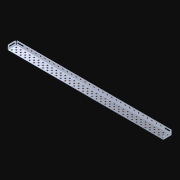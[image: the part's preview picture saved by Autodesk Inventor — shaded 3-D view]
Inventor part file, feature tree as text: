
AUTODESK INVENTOR PART (.ipt)
format: ipt  version: 2021 (Build 250183000, 183)  size: 2,035,200 bytes
history: native  units: in
note: dims shown in document units (in); Inventor stores cm internally (conversion verified against a paired STEP export)
features: other x136, extrude x135, pattern_linear x3, imported_body x1
ambient origin geometry x8: Origin, YZ Plane, XZ Plane, XY Plane, X Axis, Y Axis, Z Axis, Center Point
bodies: Body1 (feature_tree), Body2 (feature_tree), Body3 (feature_tree), Body4 (feature_tree), Body5 (feature_tree), Body6 (feature_tree), Body7 (feature_tree), Body8 (feature_tree), Body9 (feature_tree), Body10 (feature_tree), Body11 (feature_tree), Body12 (feature_tree), Body13 (feature_tree), Body14 (feature_tree), Body15 (feature_tree), Body16 (feature_tree), Body17 (feature_tree), Body18 (feature_tree), Body19 (feature_tree), Body20 (feature_tree), Body21 (feature_tree), Body22 (feature_tree), Body23 (feature_tree), Body24 (feature_tree), Body25 (feature_tree), Body26 (feature_tree), Body27 (feature_tree), Body28 (feature_tree), Body29 (feature_tree), Body30 (feature_tree), Body31 (feature_tree), Body32 (feature_tree), Body33 (feature_tree), Body34 (feature_tree), Body35 (feature_tree), Body36 (feature_tree), Body37 (feature_tree), Body38 (feature_tree), Body39 (feature_tree), Body40 (feature_tree), Body41 (feature_tree), Body42 (feature_tree), Body43 (feature_tree), Body44 (feature_tree), Body45 (feature_tree), Body46 (feature_tree), Body47 (feature_tree), Body48 (feature_tree), Body49 (feature_tree), Body50 (feature_tree), Body51 (feature_tree), Body52 (feature_tree), Body53 (feature_tree), Body54 (feature_tree), Body55 (feature_tree), Body56 (feature_tree), Body57 (feature_tree), Body58 (feature_tree), Body59 (feature_tree), Body60 (feature_tree), Body61 (feature_tree), Body62 (feature_tree), Body63 (feature_tree), Body64 (feature_tree), Body65 (feature_tree), Body66 (feature_tree), Body67 (feature_tree), Body68 (feature_tree), Body69 (feature_tree), Body70 (feature_tree), Body71 (feature_tree), Body72 (feature_tree), Body73 (feature_tree), Body74 (feature_tree), Body75 (feature_tree), Body76 (feature_tree), Body77 (feature_tree), Body78 (feature_tree), Body79 (feature_tree), Body80 (feature_tree), Body81 (feature_tree), Body82 (feature_tree), Body83 (feature_tree), Body84 (feature_tree), Body85 (feature_tree), Body86 (feature_tree), Body87 (feature_tree), Body88 (feature_tree), Body89 (feature_tree), Body90 (feature_tree), Body91 (feature_tree), Body92 (feature_tree), Body93 (feature_tree), Body94 (feature_tree), Body95 (feature_tree), Body96 (feature_tree), Body97 (feature_tree), Body98 (feature_tree), Body99 (feature_tree), Body100 (feature_tree), Body101 (feature_tree), Body102 (feature_tree), Body103 (feature_tree), Body104 (feature_tree), Body105 (feature_tree), Body106 (feature_tree), Body107 (feature_tree), Body108 (feature_tree), Body109 (feature_tree), Body110 (feature_tree), Body111 (feature_tree), Body112 (feature_tree), Body113 (feature_tree), Body114 (feature_tree), Body115 (feature_tree), Body116 (feature_tree), Body117 (feature_tree), Body118 (feature_tree), Body119 (feature_tree), Body120 (feature_tree), Body121 (feature_tree), Body122 (feature_tree), Body123 (feature_tree), Body124 (feature_tree), Body125 (feature_tree), Body126 (feature_tree), Body127 (feature_tree), Body128 (feature_tree), Body129 (feature_tree), Body130 (feature_tree), Body131 (feature_tree), Body132 (feature_tree), Body133 (feature_tree), Body134 (feature_tree), Body135 (feature_tree), Body136 (feature_tree)
feature tree (275):
  parser-record x1  (decoder bookkeeping rows leaked as tree rows — omitted from the tree; the rows remain in map.json)
  imported_body  "Base1"
  pattern_linear  "Rectangular Pattern1"  Spacing1=0.046in  [1 undecoded]
  pattern_linear  "Rectangular Pattern2"  Count1=35 Spacing1=0.5in
  pattern_linear  "Rectangular Pattern3"  Count1=2 Spacing1=0.5in
  other  "Srf1"
  other  "Srf2"
  other  "Srf3"
  other  "Srf4"
  other  "Srf5"
  other  "Srf6"
  other  "Srf7"
  other  "Srf8"
  other  "Srf9"
  other  "Srf10"
  other  "Srf11"
  other  "Srf12"
  other  "Srf13"
  other  "Srf14"
  other  "Srf15"
  other  "Srf16"
  other  "Srf17"
  other  "Srf18"
  other  "Srf19"
  other  "Srf20"
  other  "Srf21"
  other  "Srf22"
  other  "Srf23"
  other  "Srf24"
  other  "Srf25"
  other  "Srf26"
  other  "Srf27"
  other  "Srf28"
  other  "Srf29"
  other  "Srf30"
  other  "Srf31"
  other  "Srf32"
  other  "Srf33"
  other  "Srf34"
  other  "Srf35"
  other  "Srf36"
  other  "Srf37"
  other  "Srf38"
  other  "Srf39"
  other  "Srf40"
  other  "Srf41"
  other  "Srf42"
  other  "Srf43"
  other  "Srf44"
  other  "Srf45"
  other  "Srf46"
  other  "Srf47"
  other  "Srf48"
  other  "Srf49"
  other  "Srf50"
  other  "Srf51"
  other  "Srf52"
  other  "Srf53"
  other  "Srf54"
  other  "Srf55"
  other  "Srf56"
  other  "Srf57"
  other  "Srf58"
  other  "Srf59"
  other  "Srf60"
  other  "Srf61"
  other  "Srf62"
  other  "Srf63"
  other  "Srf64"
  other  "Srf65"
  other  "Srf66"
  other  "Srf67"
  other  "Srf68"
  other  "Srf69"
  other  "Srf70"
  other  "Srf71"
  other  "Srf72"
  other  "Srf73"
  other  "Srf74"
  other  "Srf75"
  other  "Srf76"
  other  "Srf77"
  other  "Srf78"
  other  "Srf79"
  other  "Srf80"
  other  "Srf81"
  other  "Srf82"
  other  "Srf83"
  other  "Srf84"
  other  "Srf85"
  other  "Srf86"
  other  "Srf87"
  other  "Srf88"
  other  "Srf89"
  other  "Srf90"
  other  "Srf91"
  other  "Srf92"
  other  "Srf93"
  other  "Srf94"
  other  "Srf95"
  other  "Srf96"
  other  "Srf97"
  other  "Srf98"
  other  "Srf99"
  other  "Srf100"
  other  "Srf101"
  other  "Srf102"
  other  "Srf103"
  other  "Srf104"
  other  "Srf105"
  other  "Srf106"
  other  "Srf107"
  other  "Srf108"
  other  "Srf109"
  other  "Srf110"
  other  "Srf111"
  other  "Srf112"
  other  "Srf113"
  other  "Srf114"
  other  "Srf115"
  other  "Srf116"
  other  "Srf117"
  other  "Srf118"
  other  "Srf119"
  other  "Srf120"
  other  "Srf121"
  other  "Srf122"
  other  "Srf123"
  other  "Srf124"
  other  "Srf125"
  other  "Srf126"
  other  "Srf127"
  other  "Srf128"
  other  "Srf129"
  other  "Srf130"
  other  "Srf131"
  other  "Srf132"
  other  "Srf133"
  other  "Srf134"
  other  "Srf135"
  extrude  "ExtrusionSrf1"  Depth=0.046in TaperAngle=0.0deg
  extrude  "ExtrusionSrf71"  Depth=0.5in
  extrude  "ExtrusionSrf105"  Depth=0.046in TaperAngle=0.0deg
  extrude  "ExtrusionSrf2"  Depth=0.5in
  extrude  "ExtrusionSrf3"  [1 undecoded]
  extrude  "ExtrusionSrf4"  [1 undecoded]
  extrude  "ExtrusionSrf5"  [1 undecoded]
  extrude  "ExtrusionSrf6"  [1 undecoded]
  extrude  "ExtrusionSrf7"  [1 undecoded]
  extrude  "ExtrusionSrf8"  [1 undecoded]
  extrude  "ExtrusionSrf9"  [1 undecoded]
  extrude  "ExtrusionSrf10"  [1 undecoded]
  extrude  "ExtrusionSrf11"  [1 undecoded]
  extrude  "ExtrusionSrf12"  [1 undecoded]
  extrude  "ExtrusionSrf13"  [1 undecoded]
  extrude  "ExtrusionSrf14"  [1 undecoded]
  extrude  "ExtrusionSrf15"  [1 undecoded]
  extrude  "ExtrusionSrf16"  [1 undecoded]
  extrude  "ExtrusionSrf17"  [1 undecoded]
  extrude  "ExtrusionSrf18"  [1 undecoded]
  extrude  "ExtrusionSrf19"  [1 undecoded]
  extrude  "ExtrusionSrf20"  [1 undecoded]
  extrude  "ExtrusionSrf21"  [1 undecoded]
  extrude  "ExtrusionSrf22"  [1 undecoded]
  extrude  "ExtrusionSrf23"  [1 undecoded]
  extrude  "ExtrusionSrf24"  [1 undecoded]
  extrude  "ExtrusionSrf25"  [1 undecoded]
  extrude  "ExtrusionSrf26"  [1 undecoded]
  extrude  "ExtrusionSrf27"  [1 undecoded]
  extrude  "ExtrusionSrf28"  [1 undecoded]
  extrude  "ExtrusionSrf29"  [1 undecoded]
  extrude  "ExtrusionSrf30"  [1 undecoded]
  extrude  "ExtrusionSrf31"  [1 undecoded]
  extrude  "ExtrusionSrf32"  [1 undecoded]
  extrude  "ExtrusionSrf33"  [1 undecoded]
  extrude  "ExtrusionSrf34"  [1 undecoded]
  extrude  "ExtrusionSrf35"  [1 undecoded]
  extrude  "ExtrusionSrf36"  [1 undecoded]
  extrude  "ExtrusionSrf37"  [1 undecoded]
  extrude  "ExtrusionSrf38"  [1 undecoded]
  extrude  "ExtrusionSrf39"  [1 undecoded]
  extrude  "ExtrusionSrf40"  [1 undecoded]
  extrude  "ExtrusionSrf41"  [1 undecoded]
  extrude  "ExtrusionSrf42"  [1 undecoded]
  extrude  "ExtrusionSrf43"  [1 undecoded]
  extrude  "ExtrusionSrf44"  [1 undecoded]
  extrude  "ExtrusionSrf45"  [1 undecoded]
  extrude  "ExtrusionSrf46"  [1 undecoded]
  extrude  "ExtrusionSrf47"  [1 undecoded]
  extrude  "ExtrusionSrf48"  [1 undecoded]
  extrude  "ExtrusionSrf49"  [1 undecoded]
  extrude  "ExtrusionSrf50"  [1 undecoded]
  extrude  "ExtrusionSrf51"  [1 undecoded]
  extrude  "ExtrusionSrf52"  [1 undecoded]
  extrude  "ExtrusionSrf53"  [1 undecoded]
  extrude  "ExtrusionSrf54"  [1 undecoded]
  extrude  "ExtrusionSrf55"  [1 undecoded]
  extrude  "ExtrusionSrf56"  [1 undecoded]
  extrude  "ExtrusionSrf57"  [1 undecoded]
  extrude  "ExtrusionSrf58"  [1 undecoded]
  extrude  "ExtrusionSrf59"  [1 undecoded]
  extrude  "ExtrusionSrf60"  [1 undecoded]
  extrude  "ExtrusionSrf61"  [1 undecoded]
  extrude  "ExtrusionSrf62"  [1 undecoded]
  extrude  "ExtrusionSrf63"  [1 undecoded]
  extrude  "ExtrusionSrf64"  [1 undecoded]
  extrude  "ExtrusionSrf65"  [1 undecoded]
  extrude  "ExtrusionSrf66"  [1 undecoded]
  extrude  "ExtrusionSrf67"  [1 undecoded]
  extrude  "ExtrusionSrf68"  [1 undecoded]
  extrude  "ExtrusionSrf69"  [1 undecoded]
  extrude  "ExtrusionSrf70"  [1 undecoded]
  extrude  "ExtrusionSrf72"  [1 undecoded]
  extrude  "ExtrusionSrf73"  [1 undecoded]
  extrude  "ExtrusionSrf74"  [1 undecoded]
  extrude  "ExtrusionSrf75"  [1 undecoded]
  extrude  "ExtrusionSrf76"  [1 undecoded]
  extrude  "ExtrusionSrf77"  [1 undecoded]
  extrude  "ExtrusionSrf78"  [1 undecoded]
  extrude  "ExtrusionSrf79"  [1 undecoded]
  extrude  "ExtrusionSrf80"  [1 undecoded]
  extrude  "ExtrusionSrf81"  [1 undecoded]
  extrude  "ExtrusionSrf82"  [1 undecoded]
  extrude  "ExtrusionSrf83"  [1 undecoded]
  extrude  "ExtrusionSrf84"  [1 undecoded]
  extrude  "ExtrusionSrf85"  [1 undecoded]
  extrude  "ExtrusionSrf86"  [1 undecoded]
  extrude  "ExtrusionSrf87"  [1 undecoded]
  extrude  "ExtrusionSrf88"  [1 undecoded]
  extrude  "ExtrusionSrf89"  [1 undecoded]
  extrude  "ExtrusionSrf90"  [1 undecoded]
  extrude  "ExtrusionSrf91"  [1 undecoded]
  extrude  "ExtrusionSrf92"  [1 undecoded]
  extrude  "ExtrusionSrf93"  [1 undecoded]
  extrude  "ExtrusionSrf94"  [1 undecoded]
  extrude  "ExtrusionSrf95"  [1 undecoded]
  extrude  "ExtrusionSrf96"  [1 undecoded]
  extrude  "ExtrusionSrf97"  [1 undecoded]
  extrude  "ExtrusionSrf98"  [1 undecoded]
  extrude  "ExtrusionSrf99"  [1 undecoded]
  extrude  "ExtrusionSrf100"  [1 undecoded]
  extrude  "ExtrusionSrf101"  [1 undecoded]
  extrude  "ExtrusionSrf102"  [1 undecoded]
  extrude  "ExtrusionSrf103"  [1 undecoded]
  extrude  "ExtrusionSrf104"  [1 undecoded]
  extrude  "ExtrusionSrf106"  [1 undecoded]
  extrude  "ExtrusionSrf107"  [1 undecoded]
  extrude  "ExtrusionSrf108"  [1 undecoded]
  extrude  "ExtrusionSrf109"  [1 undecoded]
  extrude  "ExtrusionSrf110"  [1 undecoded]
  extrude  "ExtrusionSrf111"  [1 undecoded]
  extrude  "ExtrusionSrf112"  [1 undecoded]
  extrude  "ExtrusionSrf113"  [1 undecoded]
  extrude  "ExtrusionSrf114"  [1 undecoded]
  extrude  "ExtrusionSrf115"  [1 undecoded]
  extrude  "ExtrusionSrf116"  [1 undecoded]
  extrude  "ExtrusionSrf117"  [1 undecoded]
  extrude  "ExtrusionSrf118"  [1 undecoded]
  extrude  "ExtrusionSrf119"  [1 undecoded]
  extrude  "ExtrusionSrf120"  [1 undecoded]
  extrude  "ExtrusionSrf121"  [1 undecoded]
  extrude  "ExtrusionSrf122"  [1 undecoded]
  extrude  "ExtrusionSrf123"  [1 undecoded]
  extrude  "ExtrusionSrf124"  [1 undecoded]
  extrude  "ExtrusionSrf125"  [1 undecoded]
  extrude  "ExtrusionSrf126"  [1 undecoded]
  extrude  "ExtrusionSrf127"  [1 undecoded]
  extrude  "ExtrusionSrf128"  [1 undecoded]
  extrude  "ExtrusionSrf129"  [1 undecoded]
  extrude  "ExtrusionSrf130"  [1 undecoded]
  extrude  "ExtrusionSrf131"  [1 undecoded]
  extrude  "ExtrusionSrf132"  [1 undecoded]
  extrude  "ExtrusionSrf133"  [1 undecoded]
  extrude  "ExtrusionSrf134"  [1 undecoded]
  extrude  "ExtrusionSrf135"  [1 undecoded]
note: 132 required parameter values undecoded (feature->parameter linkage not recoverable at this tier; creation-order binding heuristic only, values carry confidence <= 0.55)
